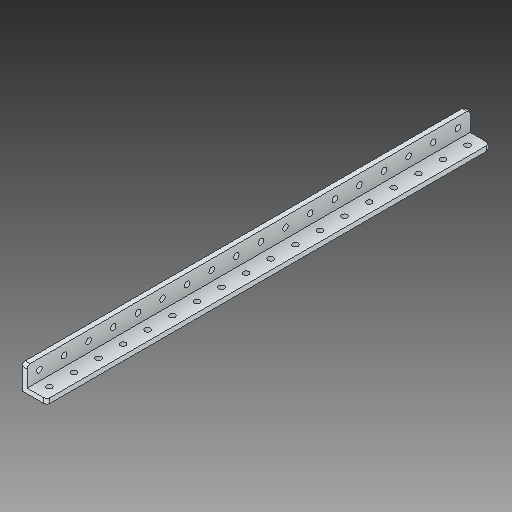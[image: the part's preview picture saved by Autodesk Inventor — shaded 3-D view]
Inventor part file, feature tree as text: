
AUTODESK INVENTOR PART (.ipt)
format: ipt  version: 2018 (Build 220112000, 112)  size: 160,768 bytes
history: native  units: in
note: dims shown in document units (in); Inventor stores cm internally (conversion verified against a paired STEP export)
features: fillet x1
ambient origin geometry x8: Origin, YZ Plane, XZ Plane, XY Plane, X Axis, Y Axis, Z Axis, Center Point
bodies: Solid1 (feature_tree)
feature tree (1):
  fillet  "Fillet1"  [1 undecoded]
note: 1 required parameter value undecoded (feature->parameter linkage not recoverable at this tier; creation-order binding heuristic only, values carry confidence <= 0.55)
